# Revit family: RAUPIANO PLUS Bend
name_source: partatom
category: Pipe Fittings
revit_build: Autodesk Revit MEP 2012 (Build: 20110309_2315(x64)
units: mm (PartAtom-declared; Revit-internal decimal feet)

## types (1)
- Standard
    A1 = 123064-001
    A10 = 121144-001
    A11 = 121154-001
    A12 = 121164-001
    A13 = 121174-001
    A14 = 121184-001
    A15 = 123384-001
    A16 = 123394-001
    A17 = 123404-001
    A18 = 123414-001
    A19 = 123424-001
    A2 = 123074-001
    A20 = 123434-001
    A21 = 123444-001
    A22 = 123454-001
    A23 = 123464-001
    A24 = 123474-001
    A25 = 123484-001
    A26 = 123494-001
    A27 = 123504-001
    A28 = 123514-001
    A29 = 124028-001
    A3 = 123084-001
    A30 = 124029-001
    A31 = 123654-001
    A32 = 123664-001
    A4 = 123094-001
    A5 = 121094-001
    A6 = 121104-001
    A7 = 121114-001
    A8 = 121124-001
    A9 = 121134-001
    Description = REHAU RAUPIANO PLUS bend
    Fail = No article found
    K Coefficient Table = Regular 45, 90 and 180 Elbow
    Lookup Table Name = RAUPIANO Bend.csv
    Loss Method = K Coefficient from Table
    M1 = 11230641001
    M10 = 11211441001
    M11 = 11211541001
    M12 = 11211641001
    M13 = 11211741001
    M14 = 11211841001
    M15 = 11233841001
    M16 = 11233941001
    M17 = 11234041001
    M18 = 11234141001
    M19 = 11234241001
    M2 = 11230741001
    M20 = 11234341001
    M21 = 11234441001
    M22 = 11234541001
    M23 = 11234641001
    M24 = 11234741001
    M25 = 11234841001
    M26 = 11234941001
    M27 = 11235041001
    M28 = 11235141001
    M29 = 11240281001
    M3 = 11230841001
    M30 = 11240291001
    M31 = 11236541001
    M32 = 11236641001
    M4 = 11230941001
    M5 = 11210941001
    M6 = 11211041001
    M7 = 11211141001
    M8 = 11211241001
    M9 = 11211341001
    Manufacturer = REHAU
    T1 = DN 40 - 15 degree
    T10 = DN 75 - 15 degree
    T11 = DN 75 - 30 degree
    T12 = DN 75 - 45 degree
    T13 = DN 75 - 67 degree
    T14 = DN 75 - 87 degree
    T15 = DN 90 - 15 degree
    T16 = DN 90 - 30 degree
    T17 = DN 90 - 45 degree
    T18 = DN 90 - 87 degree
    T19 = DN 110 - 15 degree
    T2 = DN 40 - 30 degree
    T20 = DN 110 - 30 degree
    T21 = DN 110 - 45 degree
    T22 = DN 110 - 67 degree
    T23 = DN 110 - 87 degree
    T24 = DN 125 - 15 degree
    T25 = DN 125 - 30 degree
    T26 = DN 125 - 45 degree
    T27 = DN 125 - 67 degree
    T28 = DN 125 - 87 degree
    T29 = DN 160 - 45 degree
    T3 = DN 40 - 45 degree
    T30 = DN 160 - 87 degree
    T31 = DN 200 - 45 degree
    T32 = DN 200 - 87 degree
    T4 = DN 40 - 87 degree
    T5 = DN 50 - 15 degree
    T6 = DN 50 - 30 degree
    T7 = DN 50 - 45 degree
    T8 = DN 50 - 67 degree
    T9 = DN 50 - 87 degree
    Type Comments = RAU-PP; Push-fit; White
